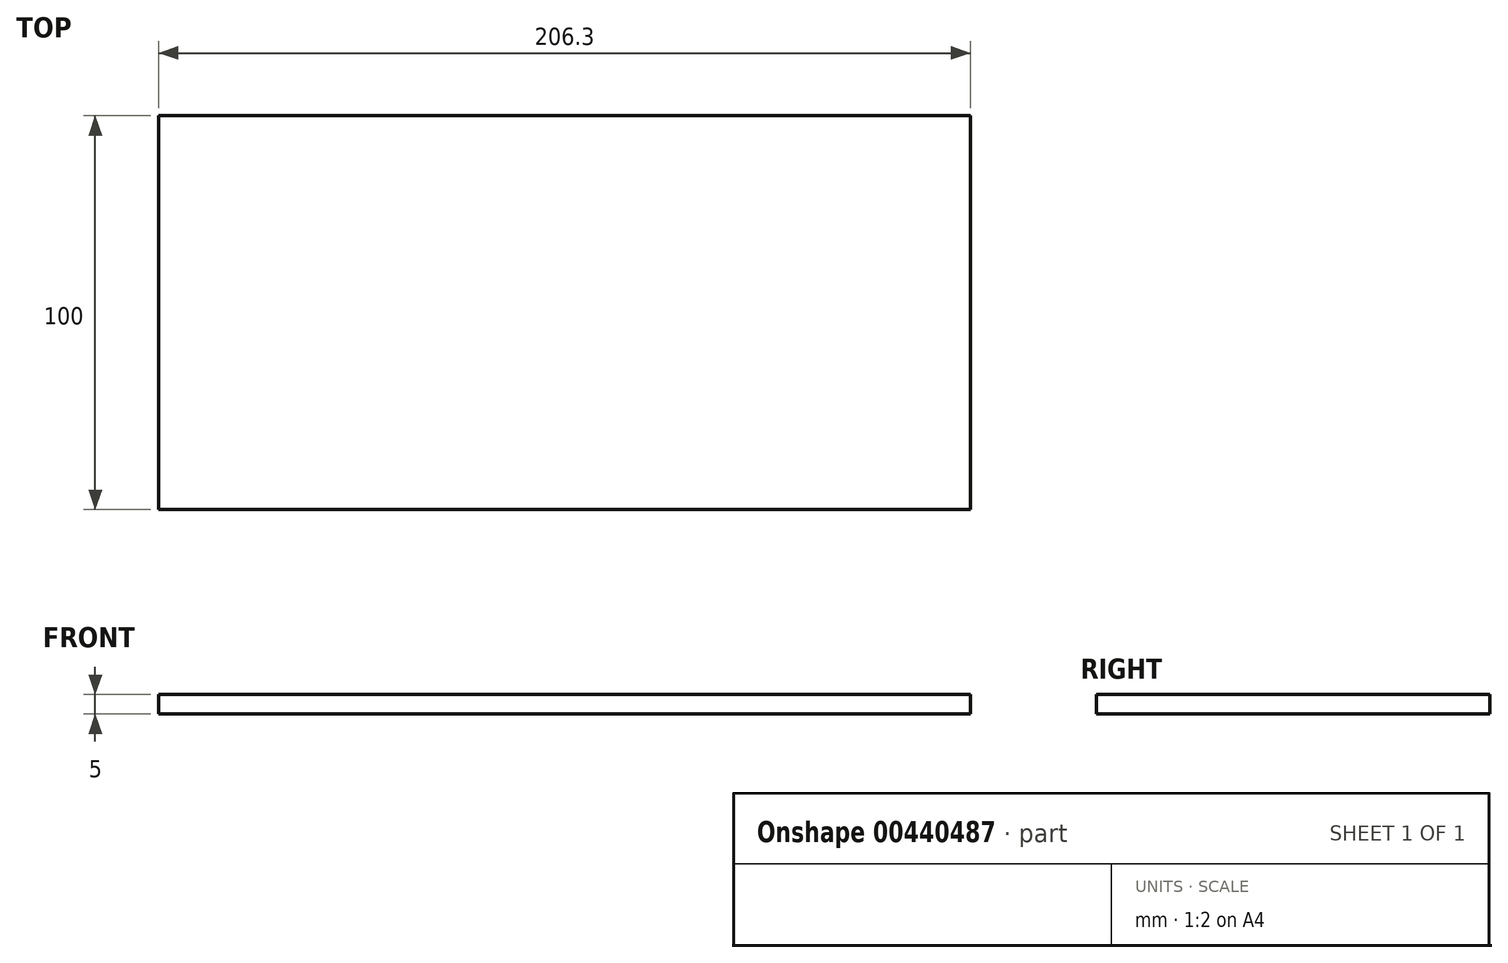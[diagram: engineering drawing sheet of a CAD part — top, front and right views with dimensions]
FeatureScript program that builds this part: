
annotation { "Feature Type Name" : "Feature", "Feature Type Description" : "" }
export const myFeature = defineFeature(function(context is Context, id is Id, definition is map)
    precondition{}
    {
        {
            var Q0;
            Q0=qCreatedBy(makeId("Top.planeOp"),FACE);
            var sketch = newSketch(context, id + "F0", { "sketchPlane" : qUnion([Q0])});
            skLineSegment(sketch, "E0.bottom", {"start": v(-103.15, -50) * mm, "end": v(103.15, -50) * mm});
            skLineSegment(sketch, "E0.top", {"start": v(-103.15, 50) * mm, "end": v(103.15, 50) * mm});
            skLineSegment(sketch, "E0.left", {"start": v(-103.15, -50) * mm, "end": v(-103.15, 50) * mm});
            skLineSegment(sketch, "E0.right", {"start": v(103.15, -50) * mm, "end": v(103.15, 50) * mm});
            skPoint(sketch, "E0.middle", {"position": v(0, 0) * mm});
            skSolve(sketch);
        }
        {
            var Q0;
            Q0 = qSketchRegion(id + "F0", true);
            extrude(context, id + "F1", {"entities" : qUnion([Q0]), "depth" : 5 * mm});
        }
    });
